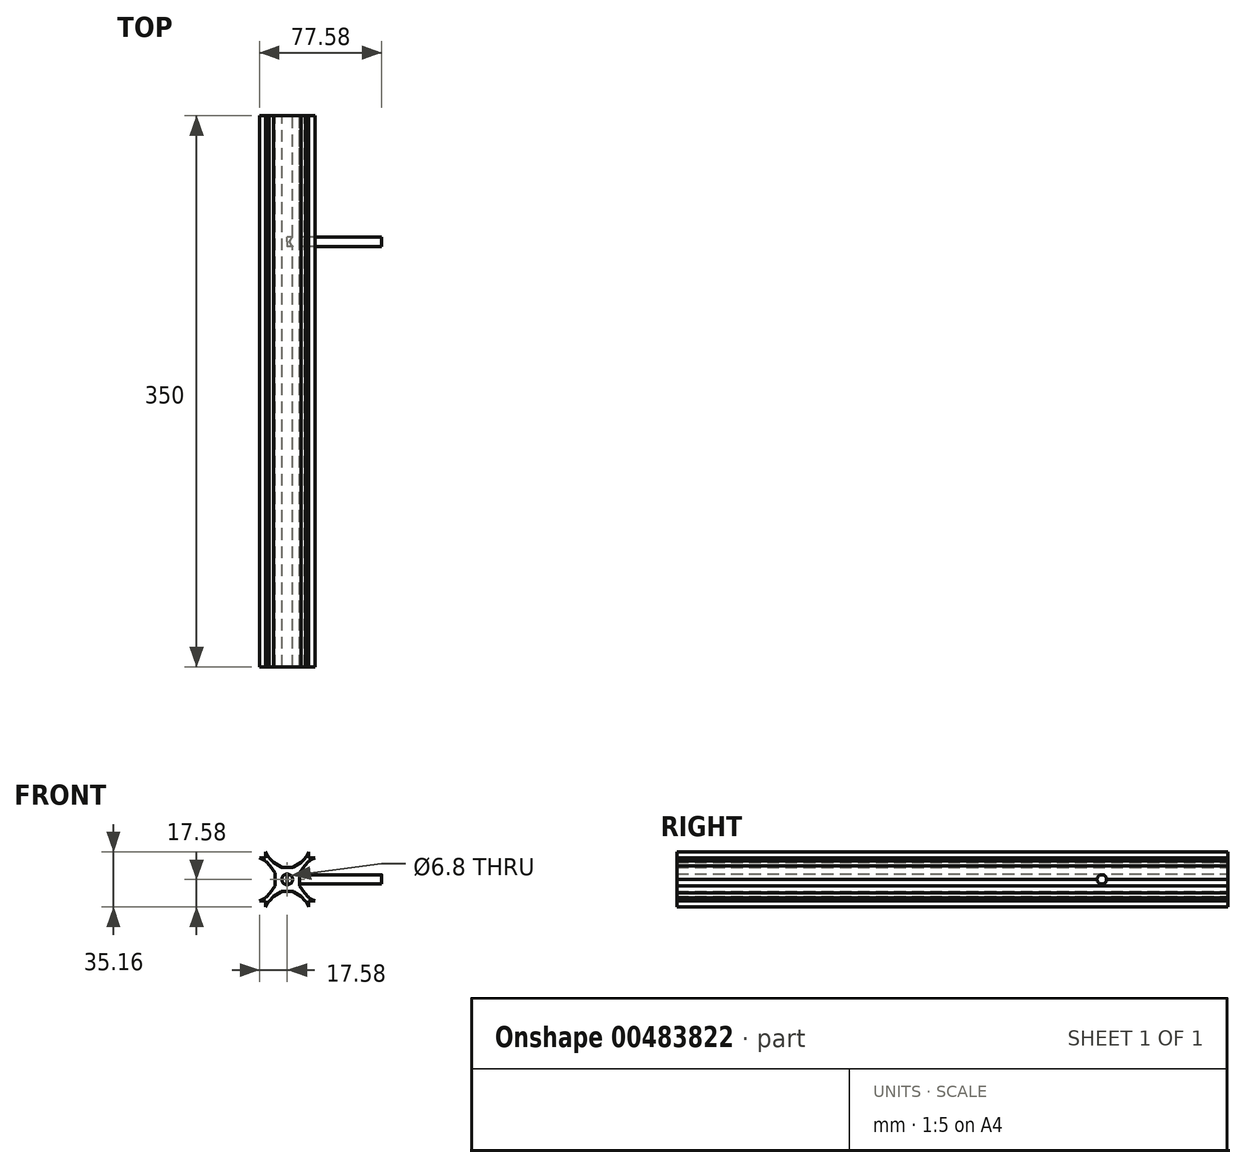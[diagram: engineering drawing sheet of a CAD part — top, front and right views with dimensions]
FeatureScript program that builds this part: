
annotation { "Feature Type Name" : "Feature", "Feature Type Description" : "" }
export const myFeature = defineFeature(function(context is Context, id is Id, definition is map)
    precondition{}
    {
        {
            var Q0;
            Q0=qCreatedBy(makeId("Front.planeOp"),FACE);
            var sketch = newSketch(context, id + "F0", { "sketchPlane" : qUnion([Q0])});
            skLineSegment(sketch, "E0.bottom", {"start": v(-16.36, 18.36) * mm, "end": v(-13.65, 18.36) * mm});
            skLineSegment(sketch, "E0.top", {"start": v(-18.36, 13.65) * mm, "end": v(-13.65, 13.65) * mm});
            skLineSegment(sketch, "E0.right", {"start": v(-13.65, 18.36) * mm, "end": v(-13.65, 13.65) * mm});
            skLineSegment(sketch, "E1", {"start": v(-7.83, 4) * mm, "end": v(-10.88, 8.69) * mm});
            skLineSegment(sketch, "E2", {"start": v(-10.88, 8.69) * mm, "end": v(-13.5, 11.3) * mm});
            skCircle(sketch, "E3", {"center": v(0, 0) * mm, "radius": 3.4 * mm});
            skLineSegment(sketch, "E4", {"start": v(-20, 3.4) * mm, "end": v(-19.97, 3.4) * mm});
            skLineSegment(sketch, "E5", {"start": v(-16, 3.9) * mm, "end": v(-16, 5.9) * mm});
            skLineSegment(sketch, "E6", {"start": v(-16.5, 6.4) * mm, "end": v(-17.08, 6.4) * mm});
            skFitSpline(sketch, "E7", {"points": [v(-18, 6.4) * mm, v(-18, 9.03) * mm, v(-17.04, 10.7) * mm, v(-15.02, 11.66) * mm, v(-13.85, 11.66) * mm, v(-51.55, 27.96) * mm, v(-53, 27.74) * mm], "startDerivative": vector(-2.1, 22.69) * mm, "endDerivative": vector(-5.98, -7.44) * mm});
            skArc(sketch, "E8.filletArc", {"start": v(-18.08, 7.34) * mm, "mid": v(-17.76, 6.67) * mm, "end": v(-17.08, 6.4) * mm});
            skArc(sketch, "E9.filletArc", {"start": v(-13.5, 11.3) * mm, "mid": v(-13.78, 11.5) * mm, "end": v(-14.1, 11.6) * mm});
            skLineSegment(sketch, "E10", {"start": v(-18.36, 16.36) * mm, "end": v(-18.36, 13.65) * mm});
            skPoint(sketch, "E11.visualSharp", {"position": v(-16, 6.4) * mm});
            skArc(sketch, "E11.filletArc", {"start": v(-16, 5.9) * mm, "mid": v(-16.15, 6.25) * mm, "end": v(-16.5, 6.4) * mm});
            skPoint(sketch, "E12.visualSharp", {"position": v(-16, 3.4) * mm});
            skArc(sketch, "E12.filletArc", {"start": v(-16.5, 3.4) * mm, "mid": v(-16.15, 3.55) * mm, "end": v(-16, 3.9) * mm});
            skLineSegment(sketch, "E13", {"start": v(-20, 3.9) * mm, "end": v(-20, 17) * mm});
            skArc(sketch, "E14.filletArc", {"start": v(-20, 3.9) * mm, "mid": v(-19.85, 3.55) * mm, "end": v(-19.5, 3.4) * mm});
            skLineSegment(sketch, "E15", {"start": v(-19.5, 3.4) * mm, "end": v(-16.5, 3.4) * mm});
            skPoint(sketch, "E16.visualSharp", {"position": v(-7.75, 3.88) * mm});
            skArc(sketch, "E16.filletArc", {"start": v(-7.75, 3.73) * mm, "mid": v(-7.77, 3.87) * mm, "end": v(-7.83, 4) * mm});
            skPoint(sketch, "E17.visualSharp", {"position": v(-18.36, 18.36) * mm});
            skArc(sketch, "E17.filletArc", {"start": v(-16.36, 18.36) * mm, "mid": v(-17.77, 17.77) * mm, "end": v(-18.36, 16.36) * mm});
            skPoint(sketch, "E18.visualSharp", {"position": v(-20, 20) * mm});
            skArc(sketch, "E18.filletArc", {"start": v(-17, 20) * mm, "mid": v(-19.12, 19.12) * mm, "end": v(-20, 17) * mm});
            skArc(sketch, "E19.MirrorCS", {"start": v(-7.34, 18.08) * mm, "mid": v(-6.67, 17.76) * mm, "end": v(-6.4, 17.08) * mm});
            skLineSegment(sketch, "E20.MirrorCS", {"start": v(-6.4, 16.5) * mm, "end": v(-6.4, 17.08) * mm});
            skLineSegment(sketch, "E21.MirrorCS", {"start": v(-3.9, 16) * mm, "end": v(-5.9, 16) * mm});
            skArc(sketch, "E22.MirrorCS", {"start": v(-5.9, 16) * mm, "mid": v(-6.25, 16.15) * mm, "end": v(-6.4, 16.5) * mm});
            skArc(sketch, "E23.MirrorCS", {"start": v(-11.3, 13.5) * mm, "mid": v(-11.5, 13.78) * mm, "end": v(-11.6, 14.1) * mm});
            skArc(sketch, "E24.MirrorCS", {"start": v(-3.73, 7.75) * mm, "mid": v(-3.87, 7.77) * mm, "end": v(-4, 7.83) * mm});
            skArc(sketch, "E25.MirrorCS", {"start": v(-3.4, 16.5) * mm, "mid": v(-3.55, 16.15) * mm, "end": v(-3.9, 16) * mm});
            skLineSegment(sketch, "E26.MirrorCS", {"start": v(-3.4, 19.5) * mm, "end": v(-3.4, 16.5) * mm});
            skLineSegment(sketch, "E27.MirrorCS", {"start": v(-3.4, 20) * mm, "end": v(-3.4, 19.97) * mm});
            skArc(sketch, "E28.MirrorCS", {"start": v(-3.9, 20) * mm, "mid": v(-3.55, 19.85) * mm, "end": v(-3.4, 19.5) * mm});
            skLineSegment(sketch, "E29.MirrorCS", {"start": v(-8.69, 10.88) * mm, "end": v(-11.3, 13.5) * mm});
            skArc(sketch, "E30.MirrorCS", {"start": v(-20, 17) * mm, "mid": v(-19.12, 19.12) * mm, "end": v(-17, 20) * mm});
            skArc(sketch, "E31.MirrorCS", {"start": v(-18.36, 16.36) * mm, "mid": v(-17.77, 17.77) * mm, "end": v(-16.36, 18.36) * mm});
            skFitSpline(sketch, "E32.MirrorCS", {"points": [v(-6.4, 18) * mm, v(-9.03, 18) * mm, v(-10.7, 17.04) * mm, v(-11.66, 15.02) * mm, v(-11.66, 13.85) * mm, v(-27.96, 51.55) * mm, v(-27.74, 53) * mm], "startDerivative": vector(-22.69, 2.1) * mm, "endDerivative": vector(7.44, 5.98) * mm});
            skPoint(sketch, "E33.MirrorP", {"position": v(-6.4, 16) * mm});
            skPoint(sketch, "E34.MirrorP", {"position": v(-3.88, 7.75) * mm});
            skPoint(sketch, "E35.MirrorP", {"position": v(-3.4, 16) * mm});
            skLineSegment(sketch, "E36.MirrorCS", {"start": v(-3.9, 20) * mm, "end": v(-17, 20) * mm});
            skLineSegment(sketch, "E37.MirrorCS", {"start": v(-4, 7.83) * mm, "end": v(-8.69, 10.88) * mm});
            skLineSegment(sketch, "E38.MirrorCS", {"start": v(0, 7.75) * mm, "end": v(-3.73, 7.75) * mm});
            skArc(sketch, "E39.MirrorCS", {"start": v(18.36, 16.36) * mm, "mid": v(17.77, 17.77) * mm, "end": v(16.36, 18.36) * mm});
            skLineSegment(sketch, "E40.MirrorCS", {"start": v(16.5, 6.4) * mm, "end": v(17.08, 6.4) * mm});
            skArc(sketch, "E41.MirrorCS", {"start": v(16.36, 18.36) * mm, "mid": v(17.77, 17.77) * mm, "end": v(18.36, 16.36) * mm});
            skArc(sketch, "E42.MirrorCS", {"start": v(16, 5.9) * mm, "mid": v(16.15, 6.25) * mm, "end": v(16.5, 6.4) * mm});
            skArc(sketch, "E43.MirrorCS", {"start": v(3.73, 7.75) * mm, "mid": v(3.87, 7.77) * mm, "end": v(4, 7.83) * mm});
            skPoint(sketch, "E44.MirrorP", {"position": v(18.36, 18.36) * mm});
            skArc(sketch, "E45.MirrorCS", {"start": v(13.5, 11.3) * mm, "mid": v(13.78, 11.5) * mm, "end": v(14.1, 11.6) * mm});
            skArc(sketch, "E46.MirrorCS", {"start": v(20, 3.9) * mm, "mid": v(19.85, 3.55) * mm, "end": v(19.5, 3.4) * mm});
            skArc(sketch, "E47.MirrorCS", {"start": v(7.75, 3.73) * mm, "mid": v(7.77, 3.87) * mm, "end": v(7.83, 4) * mm});
            skLineSegment(sketch, "E48.MirrorCS", {"start": v(16, 3.9) * mm, "end": v(16, 5.9) * mm});
            skArc(sketch, "E49.MirrorCS", {"start": v(3.4, 16.5) * mm, "mid": v(3.55, 16.15) * mm, "end": v(3.9, 16) * mm});
            skArc(sketch, "E50.MirrorCS", {"start": v(5.9, 16) * mm, "mid": v(6.25, 16.15) * mm, "end": v(6.4, 16.5) * mm});
            skArc(sketch, "E51.MirrorCS", {"start": v(18.08, 7.34) * mm, "mid": v(17.76, 6.67) * mm, "end": v(17.08, 6.4) * mm});
            skLineSegment(sketch, "E52.MirrorCS", {"start": v(3.9, 16) * mm, "end": v(5.9, 16) * mm});
            skArc(sketch, "E53.MirrorCS", {"start": v(16.5, 3.4) * mm, "mid": v(16.15, 3.55) * mm, "end": v(16, 3.9) * mm});
            skArc(sketch, "E54.MirrorCS", {"start": v(11.3, 13.5) * mm, "mid": v(11.5, 13.78) * mm, "end": v(11.6, 14.1) * mm});
            skLineSegment(sketch, "E55.MirrorCS", {"start": v(20, 3.4) * mm, "end": v(19.97, 3.4) * mm});
            skLineSegment(sketch, "E56.MirrorCS", {"start": v(6.4, 16.5) * mm, "end": v(6.4, 17.08) * mm});
            skArc(sketch, "E57.MirrorCS", {"start": v(3.9, 20) * mm, "mid": v(3.55, 19.85) * mm, "end": v(3.4, 19.5) * mm});
            skLineSegment(sketch, "E58.MirrorCS", {"start": v(3.4, 20) * mm, "end": v(3.4, 19.97) * mm});
            skArc(sketch, "E59.MirrorCS", {"start": v(7.34, 18.08) * mm, "mid": v(6.67, 17.76) * mm, "end": v(6.4, 17.08) * mm});
            skPoint(sketch, "E60.MirrorP", {"position": v(16, 6.4) * mm});
            skArc(sketch, "E61.MirrorCS", {"start": v(20, 17) * mm, "mid": v(19.12, 19.12) * mm, "end": v(17, 20) * mm});
            skPoint(sketch, "E62.MirrorP", {"position": v(20, 20) * mm});
            skFitSpline(sketch, "E63.MirrorCS", {"points": [v(6.4, 18) * mm, v(9.03, 18) * mm, v(10.7, 17.04) * mm, v(11.66, 15.02) * mm, v(11.66, 13.85) * mm, v(27.96, 51.55) * mm, v(27.74, 53) * mm], "startDerivative": vector(22.69, 2.1) * mm, "endDerivative": vector(-7.44, 5.98) * mm});
            skLineSegment(sketch, "E64.MirrorCS", {"start": v(18.36, 13.65) * mm, "end": v(13.65, 13.65) * mm});
            skFitSpline(sketch, "E65.MirrorCS", {"points": [v(18, 6.4) * mm, v(18, 9.03) * mm, v(17.04, 10.7) * mm, v(15.02, 11.66) * mm, v(13.85, 11.66) * mm, v(51.55, 27.96) * mm, v(53, 27.74) * mm], "startDerivative": vector(2.1, 22.69) * mm, "endDerivative": vector(5.98, -7.44) * mm});
            skLineSegment(sketch, "E66.MirrorCS", {"start": v(16.36, 18.36) * mm, "end": v(13.65, 18.36) * mm});
            skLineSegment(sketch, "E67.MirrorCS", {"start": v(13.65, 18.36) * mm, "end": v(13.65, 13.65) * mm});
            skLineSegment(sketch, "E68.MirrorCS", {"start": v(19.5, 3.4) * mm, "end": v(16.5, 3.4) * mm});
            skLineSegment(sketch, "E69.MirrorCS", {"start": v(18.36, 16.36) * mm, "end": v(18.36, 13.65) * mm});
            skPoint(sketch, "E70.MirrorP", {"position": v(16, 3.4) * mm});
            skPoint(sketch, "E71.MirrorP", {"position": v(3.4, 16) * mm});
            skLineSegment(sketch, "E72.MirrorCS", {"start": v(8.69, 10.88) * mm, "end": v(11.3, 13.5) * mm});
            skArc(sketch, "E73.MirrorCS", {"start": v(17, 20) * mm, "mid": v(19.12, 19.12) * mm, "end": v(20, 17) * mm});
            skLineSegment(sketch, "E74.MirrorCS", {"start": v(3.4, 19.5) * mm, "end": v(3.4, 16.5) * mm});
            skPoint(sketch, "E75.MirrorP", {"position": v(7.75, 3.88) * mm});
            skPoint(sketch, "E76.MirrorP", {"position": v(3.88, 7.75) * mm});
            skLineSegment(sketch, "E77.MirrorCS", {"start": v(20, 3.9) * mm, "end": v(20, 17) * mm});
            skLineSegment(sketch, "E78.MirrorCS", {"start": v(0, 7.75) * mm, "end": v(3.73, 7.75) * mm});
            skLineSegment(sketch, "E79.MirrorCS", {"start": v(4, 7.83) * mm, "end": v(8.69, 10.88) * mm});
            skLineSegment(sketch, "E80.MirrorCS", {"start": v(7.83, 4) * mm, "end": v(10.88, 8.69) * mm});
            skLineSegment(sketch, "E81.MirrorCS", {"start": v(3.9, 20) * mm, "end": v(17, 20) * mm});
            skLineSegment(sketch, "E82.MirrorCS", {"start": v(7.75, 0) * mm, "end": v(7.75, 3.73) * mm});
            skLineSegment(sketch, "E83.MirrorCS", {"start": v(10.88, 8.69) * mm, "end": v(13.5, 11.3) * mm});
            skPoint(sketch, "E84.MirrorP", {"position": v(6.4, 16) * mm});
            skLineSegment(sketch, "E85.MirrorCS", {"start": v(18.36, -16.36) * mm, "end": v(18.36, -13.65) * mm});
            skLineSegment(sketch, "E86.MirrorCS", {"start": v(16.36, -18.36) * mm, "end": v(13.65, -18.36) * mm});
            skArc(sketch, "E87.MirrorCS", {"start": v(18.36, -16.36) * mm, "mid": v(17.77, -17.77) * mm, "end": v(16.36, -18.36) * mm});
            skLineSegment(sketch, "E88.MirrorCS", {"start": v(-16.36, -18.36) * mm, "end": v(-13.65, -18.36) * mm});
            skArc(sketch, "E89.MirrorCS", {"start": v(20, -17) * mm, "mid": v(19.12, -19.12) * mm, "end": v(17, -20) * mm});
            skLineSegment(sketch, "E90.MirrorCS", {"start": v(-18.36, -16.36) * mm, "end": v(-18.36, -13.65) * mm});
            skArc(sketch, "E91.MirrorCS", {"start": v(-20, -17) * mm, "mid": v(-19.12, -19.12) * mm, "end": v(-17, -20) * mm});
            skArc(sketch, "E92.MirrorCS", {"start": v(-18.36, -16.36) * mm, "mid": v(-17.77, -17.77) * mm, "end": v(-16.36, -18.36) * mm});
            skArc(sketch, "E93.MirrorCS", {"start": v(13.5, -11.3) * mm, "mid": v(13.78, -11.5) * mm, "end": v(14.1, -11.6) * mm});
            skArc(sketch, "E94.MirrorCS", {"start": v(-18.08, -7.34) * mm, "mid": v(-17.76, -6.67) * mm, "end": v(-17.08, -6.4) * mm});
            skArc(sketch, "E95.MirrorCS", {"start": v(3.73, -7.75) * mm, "mid": v(3.87, -7.77) * mm, "end": v(4, -7.83) * mm});
            skLineSegment(sketch, "E96.MirrorCS", {"start": v(-16.5, -6.4) * mm, "end": v(-17.08, -6.4) * mm});
            skArc(sketch, "E97.MirrorCS", {"start": v(16.36, -18.36) * mm, "mid": v(17.77, -17.77) * mm, "end": v(18.36, -16.36) * mm});
            skArc(sketch, "E98.MirrorCS", {"start": v(-16.36, -18.36) * mm, "mid": v(-17.77, -17.77) * mm, "end": v(-18.36, -16.36) * mm});
            skArc(sketch, "E99.MirrorCS", {"start": v(-3.73, -7.75) * mm, "mid": v(-3.87, -7.77) * mm, "end": v(-4, -7.83) * mm});
            skArc(sketch, "E100.MirrorCS", {"start": v(-16, -5.9) * mm, "mid": v(-16.15, -6.25) * mm, "end": v(-16.5, -6.4) * mm});
            skArc(sketch, "E101.MirrorCS", {"start": v(17, -20) * mm, "mid": v(19.12, -19.12) * mm, "end": v(20, -17) * mm});
            skArc(sketch, "E102.MirrorCS", {"start": v(-17, -20) * mm, "mid": v(-19.12, -19.12) * mm, "end": v(-20, -17) * mm});
            skArc(sketch, "E103.MirrorCS", {"start": v(-13.5, -11.3) * mm, "mid": v(-13.78, -11.5) * mm, "end": v(-14.1, -11.6) * mm});
            skArc(sketch, "E104.MirrorCS", {"start": v(-5.9, -16) * mm, "mid": v(-6.25, -16.15) * mm, "end": v(-6.4, -16.5) * mm});
            skLineSegment(sketch, "E105.MirrorCS", {"start": v(-3.9, -16) * mm, "end": v(-5.9, -16) * mm});
            skArc(sketch, "E106.MirrorCS", {"start": v(7.34, -18.08) * mm, "mid": v(6.67, -17.76) * mm, "end": v(6.4, -17.08) * mm});
            skLineSegment(sketch, "E107.MirrorCS", {"start": v(-6.4, -16.5) * mm, "end": v(-6.4, -17.08) * mm});
            skArc(sketch, "E108.MirrorCS", {"start": v(16, -5.9) * mm, "mid": v(16.15, -6.25) * mm, "end": v(16.5, -6.4) * mm});
            skLineSegment(sketch, "E109.MirrorCS", {"start": v(-16, -3.9) * mm, "end": v(-16, -5.9) * mm});
            skLineSegment(sketch, "E110.MirrorCS", {"start": v(-20, -3.4) * mm, "end": v(-19.97, -3.4) * mm});
            skArc(sketch, "E111.MirrorCS", {"start": v(-7.34, -18.08) * mm, "mid": v(-6.67, -17.76) * mm, "end": v(-6.4, -17.08) * mm});
            skArc(sketch, "E112.MirrorCS", {"start": v(-16.5, -3.4) * mm, "mid": v(-16.15, -3.55) * mm, "end": v(-16, -3.9) * mm});
            skArc(sketch, "E113.MirrorCS", {"start": v(-3.4, -16.5) * mm, "mid": v(-3.55, -16.15) * mm, "end": v(-3.9, -16) * mm});
            skArc(sketch, "E114.MirrorCS", {"start": v(7.75, -3.73) * mm, "mid": v(7.77, -3.87) * mm, "end": v(7.83, -4) * mm});
            skArc(sketch, "E115.MirrorCS", {"start": v(-20, -3.9) * mm, "mid": v(-19.85, -3.55) * mm, "end": v(-19.5, -3.4) * mm});
            skLineSegment(sketch, "E116.MirrorCS", {"start": v(6.4, -16.5) * mm, "end": v(6.4, -17.08) * mm});
            skArc(sketch, "E117.MirrorCS", {"start": v(5.9, -16) * mm, "mid": v(6.25, -16.15) * mm, "end": v(6.4, -16.5) * mm});
            skLineSegment(sketch, "E118.MirrorCS", {"start": v(16, -3.9) * mm, "end": v(16, -5.9) * mm});
            skLineSegment(sketch, "E119.MirrorCS", {"start": v(-19.5, -3.4) * mm, "end": v(-16.5, -3.4) * mm});
            skArc(sketch, "E120.MirrorCS", {"start": v(18.08, -7.34) * mm, "mid": v(17.76, -6.67) * mm, "end": v(17.08, -6.4) * mm});
            skPoint(sketch, "E121.MirrorP", {"position": v(18.36, -18.36) * mm});
            skLineSegment(sketch, "E122.MirrorCS", {"start": v(3.9, -16) * mm, "end": v(5.9, -16) * mm});
            skArc(sketch, "E123.MirrorCS", {"start": v(-11.3, -13.5) * mm, "mid": v(-11.5, -13.78) * mm, "end": v(-11.6, -14.1) * mm});
            skPoint(sketch, "E124.MirrorP", {"position": v(-18.36, -18.36) * mm});
            skLineSegment(sketch, "E125.MirrorCS", {"start": v(-3.4, -20) * mm, "end": v(-3.4, -19.97) * mm});
            skArc(sketch, "E126.MirrorCS", {"start": v(11.3, -13.5) * mm, "mid": v(11.5, -13.78) * mm, "end": v(11.6, -14.1) * mm});
            skArc(sketch, "E127.MirrorCS", {"start": v(16.5, -3.4) * mm, "mid": v(16.15, -3.55) * mm, "end": v(16, -3.9) * mm});
            skArc(sketch, "E128.MirrorCS", {"start": v(-7.75, -3.73) * mm, "mid": v(-7.77, -3.87) * mm, "end": v(-7.83, -4) * mm});
            skLineSegment(sketch, "E129.MirrorCS", {"start": v(16.5, -6.4) * mm, "end": v(17.08, -6.4) * mm});
            skArc(sketch, "E130.MirrorCS", {"start": v(3.4, -16.5) * mm, "mid": v(3.55, -16.15) * mm, "end": v(3.9, -16) * mm});
            skLineSegment(sketch, "E131.MirrorCS", {"start": v(3.4, -20) * mm, "end": v(3.4, -19.97) * mm});
            skLineSegment(sketch, "E132.MirrorCS", {"start": v(-10.88, -8.69) * mm, "end": v(-13.5, -11.3) * mm});
            skArc(sketch, "E133.MirrorCS", {"start": v(3.9, -20) * mm, "mid": v(3.55, -19.85) * mm, "end": v(3.4, -19.5) * mm});
            skLineSegment(sketch, "E134.MirrorCS", {"start": v(19.5, -3.4) * mm, "end": v(16.5, -3.4) * mm});
            skArc(sketch, "E135.MirrorCS", {"start": v(-3.9, -20) * mm, "mid": v(-3.55, -19.85) * mm, "end": v(-3.4, -19.5) * mm});
            skLineSegment(sketch, "E136.MirrorCS", {"start": v(-13.65, -18.36) * mm, "end": v(-13.65, -13.65) * mm});
            skLineSegment(sketch, "E137.MirrorCS", {"start": v(-3.4, -19.5) * mm, "end": v(-3.4, -16.5) * mm});
            skLineSegment(sketch, "E138.MirrorCS", {"start": v(10.88, -8.69) * mm, "end": v(13.5, -11.3) * mm});
            skLineSegment(sketch, "E139.MirrorCS", {"start": v(20, -3.4) * mm, "end": v(19.97, -3.4) * mm});
            skLineSegment(sketch, "E140.MirrorCS", {"start": v(3.4, -19.5) * mm, "end": v(3.4, -16.5) * mm});
            skArc(sketch, "E141.MirrorCS", {"start": v(20, -3.9) * mm, "mid": v(19.85, -3.55) * mm, "end": v(19.5, -3.4) * mm});
            skLineSegment(sketch, "E142.MirrorCS", {"start": v(7.83, -4) * mm, "end": v(10.88, -8.69) * mm});
            skFitSpline(sketch, "E143.MirrorCS", {"points": [v(-18, -6.4) * mm, v(-18, -9.03) * mm, v(-17.04, -10.7) * mm, v(-15.02, -11.66) * mm, v(-13.85, -11.66) * mm, v(-51.55, -27.96) * mm, v(-53, -27.74) * mm], "startDerivative": vector(-2.1, -22.69) * mm, "endDerivative": vector(-5.98, 7.44) * mm});
            skLineSegment(sketch, "E144.MirrorCS", {"start": v(-18.36, -13.65) * mm, "end": v(-13.65, -13.65) * mm});
            skFitSpline(sketch, "E145.MirrorCS", {"points": [v(-6.4, -18) * mm, v(-9.03, -18) * mm, v(-10.7, -17.04) * mm, v(-11.66, -15.02) * mm, v(-11.66, -13.85) * mm, v(-27.96, -51.55) * mm, v(-27.74, -53) * mm], "startDerivative": vector(-22.69, -2.1) * mm, "endDerivative": vector(7.44, -5.98) * mm});
            skLineSegment(sketch, "E146.MirrorCS", {"start": v(18.36, -13.65) * mm, "end": v(13.65, -13.65) * mm});
            skFitSpline(sketch, "E147.MirrorCS", {"points": [v(18, -6.4) * mm, v(18, -9.03) * mm, v(17.04, -10.7) * mm, v(15.02, -11.66) * mm, v(13.85, -11.66) * mm, v(51.55, -27.96) * mm, v(53, -27.74) * mm], "startDerivative": vector(2.1, -22.69) * mm, "endDerivative": vector(5.98, 7.44) * mm});
            skPoint(sketch, "E148.MirrorP", {"position": v(20, -20) * mm});
            skLineSegment(sketch, "E149.MirrorCS", {"start": v(-8.69, -10.88) * mm, "end": v(-11.3, -13.5) * mm});
            skPoint(sketch, "E150.MirrorP", {"position": v(-20, -20) * mm});
            skFitSpline(sketch, "E151.MirrorCS", {"points": [v(6.4, -18) * mm, v(9.03, -18) * mm, v(10.7, -17.04) * mm, v(11.66, -15.02) * mm, v(11.66, -13.85) * mm, v(27.96, -51.55) * mm, v(27.74, -53) * mm], "startDerivative": vector(22.69, -2.1) * mm, "endDerivative": vector(-7.44, -5.98) * mm});
            skLineSegment(sketch, "E152.MirrorCS", {"start": v(0, -7.75) * mm, "end": v(-3.73, -7.75) * mm});
            skLineSegment(sketch, "E153.MirrorCS", {"start": v(-20, -3.9) * mm, "end": v(-20, -17) * mm});
            skLineSegment(sketch, "E154.MirrorCS", {"start": v(-3.9, -20) * mm, "end": v(-17, -20) * mm});
            skPoint(sketch, "E155.MirrorP", {"position": v(-16, -6.4) * mm});
            skLineSegment(sketch, "E156.MirrorCS", {"start": v(13.65, -18.36) * mm, "end": v(13.65, -13.65) * mm});
            skLineSegment(sketch, "E157.MirrorCS", {"start": v(8.69, -10.88) * mm, "end": v(11.3, -13.5) * mm});
            skLineSegment(sketch, "E158.MirrorCS", {"start": v(3.9, -20) * mm, "end": v(17, -20) * mm});
            skPoint(sketch, "E159.MirrorP", {"position": v(16, -3.4) * mm});
            skLineSegment(sketch, "E160.MirrorCS", {"start": v(4, -7.83) * mm, "end": v(8.69, -10.88) * mm});
            skLineSegment(sketch, "E161.MirrorCS", {"start": v(-7.83, -4) * mm, "end": v(-10.88, -8.69) * mm});
            skPoint(sketch, "E162.MirrorP", {"position": v(16, -6.4) * mm});
            skPoint(sketch, "E163.MirrorP", {"position": v(3.4, -16) * mm});
            skPoint(sketch, "E164.MirrorP", {"position": v(-3.88, -7.75) * mm});
            skLineSegment(sketch, "E165.MirrorCS", {"start": v(20, -3.9) * mm, "end": v(20, -17) * mm});
            skPoint(sketch, "E166.MirrorP", {"position": v(6.4, -16) * mm});
            skPoint(sketch, "E167.MirrorP", {"position": v(3.88, -7.75) * mm});
            skPoint(sketch, "E168.MirrorP", {"position": v(-7.75, -3.88) * mm});
            skLineSegment(sketch, "E169.MirrorCS", {"start": v(-4, -7.83) * mm, "end": v(-8.69, -10.88) * mm});
            skPoint(sketch, "E170.MirrorP", {"position": v(7.75, -3.88) * mm});
            skPoint(sketch, "E171.MirrorP", {"position": v(-3.4, -16) * mm});
            skPoint(sketch, "E172.MirrorP", {"position": v(-6.4, -16) * mm});
            skPoint(sketch, "E173.MirrorP", {"position": v(-16, -3.4) * mm});
            skLineSegment(sketch, "E174", {"start": v(-7.75, -3.73) * mm, "end": v(-7.75, 3.73) * mm});
            skLineSegment(sketch, "E175", {"start": v(0, -7.75) * mm, "end": v(3.87, -7.75) * mm});
            skLineSegment(sketch, "E176", {"start": v(7.83, -4) * mm, "end": v(7.75, 0) * mm});
            skSolve(sketch);
        }
        {
            var Q0;
            Q0=makeQuery(id+"F0.imprint","IMPRINT",FACE,{"disambiguationData":[TD([[makeQuery(id+"F0.imprint","IMPRINT",EDGE,{"derivedFrom":sQuery(id+"F0.wireOp",EDGE,"E1")}),-1.0]])]});
            extrude(context, id + "F1", {"entities" : qUnion([Q0]), "depth" : 350 * mm});
        }
        {
            var Q0;
            Q0=qCreatedBy(makeId("Right.planeOp"),FACE);
            var sketch = newSketch(context, id + "F2", { "sketchPlane" : qUnion([Q0])});
            skLineSegment(sketch, "E177", {"start": v(0, 0) * mm, "end": v(-80, 0) * mm});
            skCircle(sketch, "E178", {"center": v(-80, 0) * mm, "radius": 3 * mm});
            skSolve(sketch);
        }
        {
            var Q0;
            Q0 = qSketchRegion(id + "F2", true);
            extrude(context, id + "F3", {"entities" : qUnion([Q0]), "operationType" : NewBodyOperationType.ADD, "depth" : 60 * mm});
        }
    });
